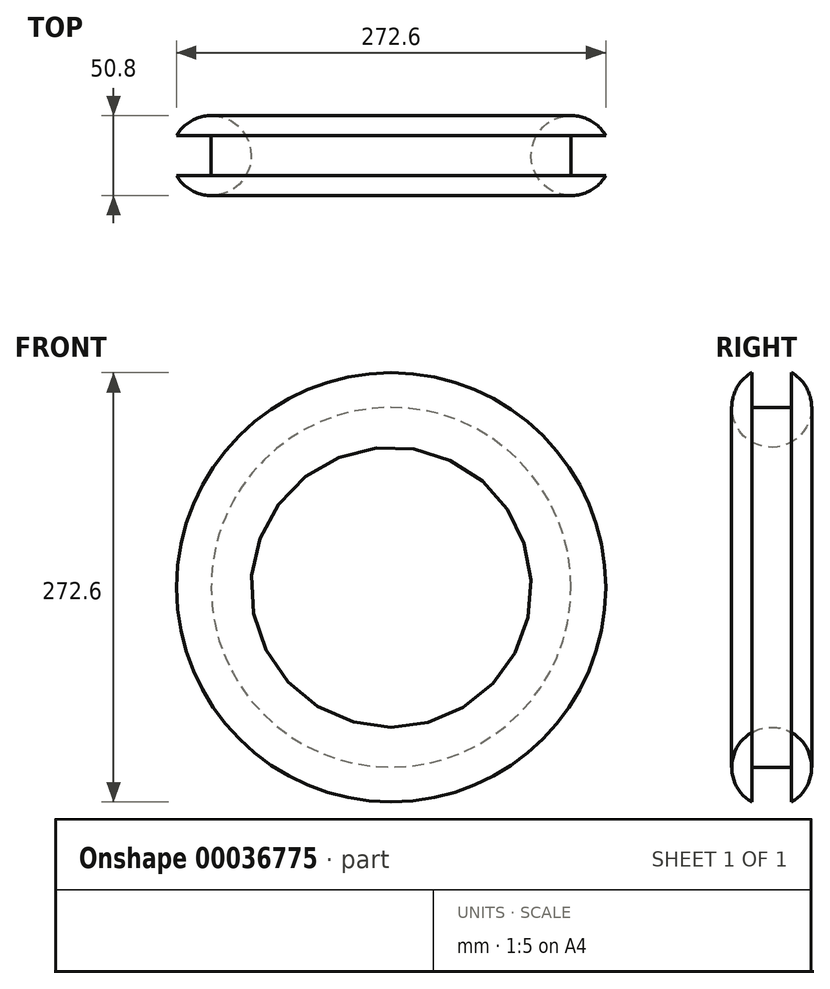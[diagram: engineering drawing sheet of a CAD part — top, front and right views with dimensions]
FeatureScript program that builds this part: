
annotation { "Feature Type Name" : "Feature", "Feature Type Description" : "" }
export const myFeature = defineFeature(function(context is Context, id is Id, definition is map)
    precondition{}
    {
        {
            var Q0;
            Q0=qCreatedBy(makeId("Top.planeOp"),FACE);
            var sketch = newSketch(context, id + "F0", { "sketchPlane" : qUnion([Q0])});
            skCircle(sketch, "E0", {"center": v(0, 0) * mm, "radius": 25.4 * mm});
            skLineSegment(sketch, "E1", {"start": v(0, 0) * mm, "end": v(0, 25.4) * mm});
            skLineSegment(sketch, "E2", {"start": v(0, 0) * mm, "end": v(0, -25.4) * mm});
            skLineSegment(sketch, "E3", {"start": v(0, -12.7) * mm, "end": v(-22, -12.7) * mm});
            skLineSegment(sketch, "E4", {"start": v(0, 12.7) * mm, "end": v(-22, 12.7) * mm});
            skPoint(sketch, "E5", {"position": v(114.3, 0) * mm});
            skLineSegment(sketch, "E6", {"start": v(114.3, 0) * mm, "end": v(114.3, 28.04) * mm});
            skLineSegment(sketch, "E7", {"start": v(114.3, 0) * mm, "end": v(114.3, -24.1) * mm});
            skSolve(sketch);
        }
        {
            var Q0;
            {var subQ0=sQuery(id+"F0.wireOp",EDGE,"E4");Q0=makeQuery(id+"F0.imprint","IMPRINT",FACE,{"disambiguationData":[TD([[makeQuery(id+"F0.imprint","IMPRINT",EDGE,{"derivedFrom":subQ0}),-1.0]])]});}
            var Q1;
            {var subQ2=sQuery(id+"F0.wireOp",EDGE,"E0");var subQ4=sQuery(id+"F0.wireOp",EDGE,"E1");var subQ7=makeQuery(id+"F0.imprint","INTERSECT",VERTEX,{"derivedFrom":[subQ2,subQ4]});Q1=makeQuery(id+"F0.imprint","IMPRINT",FACE,{"disambiguationData":[TD([[makeQuery(id+"F0.imprint","IMPRINT",EDGE,{"disambiguationData":[TD([[subQ7,1.0]])],"derivedFrom":subQ2}),1.0]])]});}
            var Q2;
            {var subQ0=sQuery(id+"F0.wireOp",EDGE,"E3");Q2=makeQuery(id+"F0.imprint","IMPRINT",FACE,{"disambiguationData":[TD([[makeQuery(id+"F0.imprint","IMPRINT",EDGE,{"derivedFrom":subQ0}),1.0]])]});}
            var Q3;
            Q3=sQuery(id+"F0.wireOp",EDGE,"E6");
            revolve(context, id + "F1", {"entities" : qUnion([Q0, Q1, Q2]), "axis" : qUnion([Q3]), "revolveType" : RevolveType.FULL});
        }
    });
